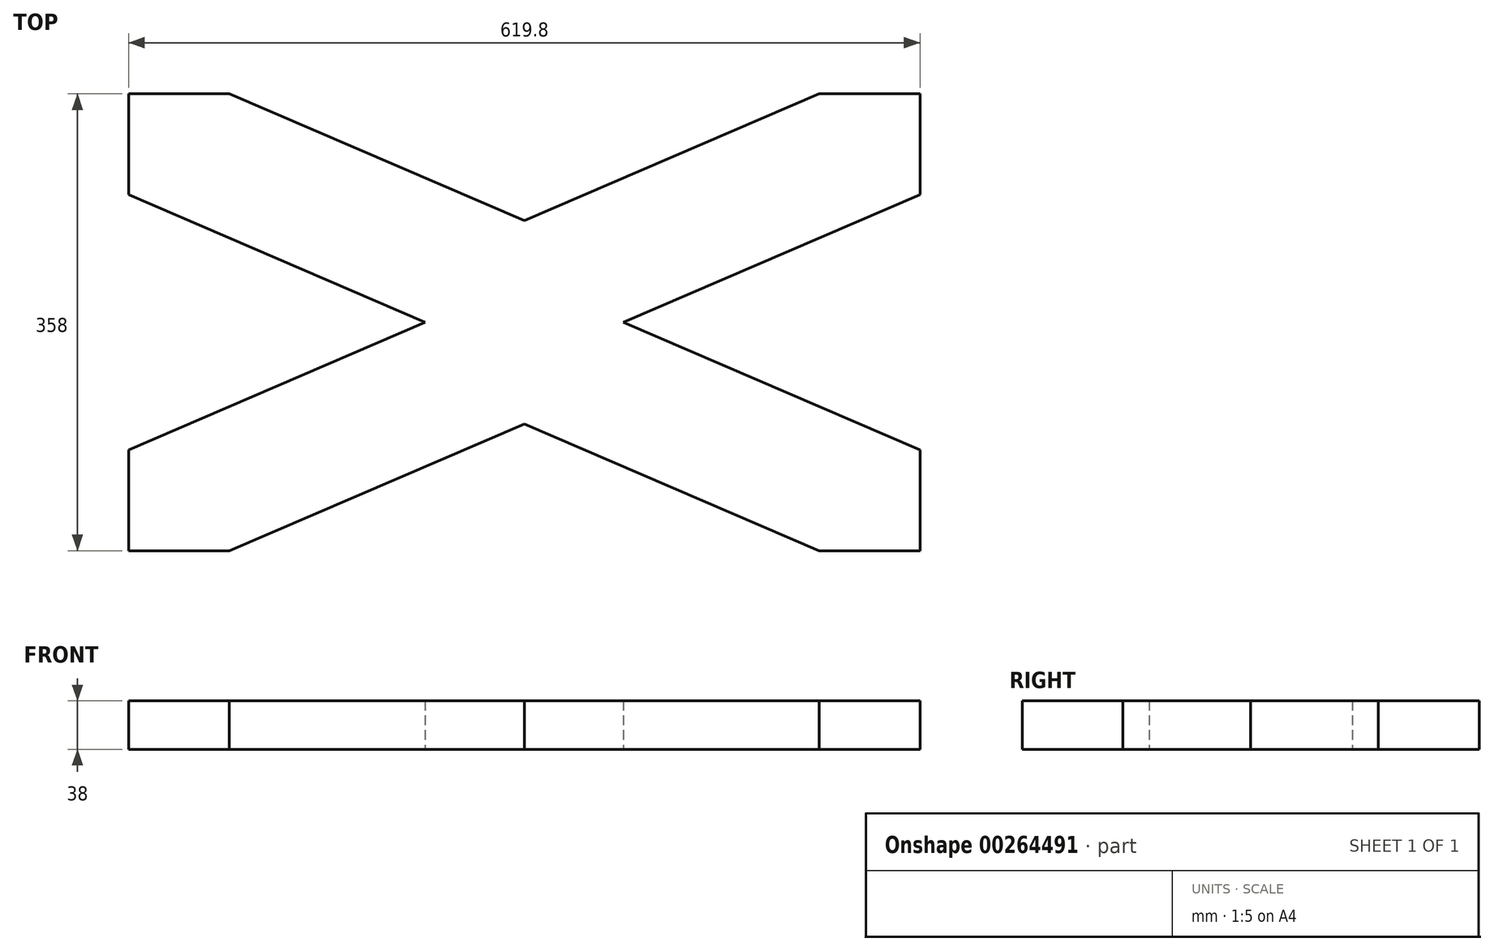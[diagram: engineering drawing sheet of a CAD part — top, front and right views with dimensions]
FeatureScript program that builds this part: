
annotation { "Feature Type Name" : "Feature", "Feature Type Description" : "" }
export const myFeature = defineFeature(function(context is Context, id is Id, definition is map)
    precondition{}
    {
        {
            var Q0;
            Q0=qCreatedBy(makeId("Top.planeOp"),FACE);
            var sketch = newSketch(context, id + "F0", { "sketchPlane" : qUnion([Q0])});
            skLineSegment(sketch, "E0.bottom", {"start": v(-309.9, 179) * mm, "end": v(309.9, 179) * mm, "construction": true});
            skLineSegment(sketch, "E0.top", {"start": v(-309.9, -179) * mm, "end": v(309.9, -179) * mm, "construction": true});
            skLineSegment(sketch, "E0.left", {"start": v(-309.9, 179) * mm, "end": v(-309.9, -179) * mm, "construction": true});
            skLineSegment(sketch, "E0.right", {"start": v(309.9, 179) * mm, "end": v(309.9, -179) * mm, "construction": true});
            skLineSegment(sketch, "E1", {"start": v(0, 179) * mm, "end": v(0, -179) * mm, "construction": true});
            skLineSegment(sketch, "E2", {"start": v(-309.9, 0) * mm, "end": v(309.9, 0) * mm, "construction": true});
            skLineSegment(sketch, "E3", {"start": v(-309.9, -100) * mm, "end": v(-309.9, -179) * mm});
            skLineSegment(sketch, "E4", {"start": v(-309.9, -179) * mm, "end": v(-230.9, -179) * mm});
            skLineSegment(sketch, "E5", {"start": v(-230.9, -179) * mm, "end": v(0, -79.65) * mm});
            skLineSegment(sketch, "E6", {"start": v(0, -79.65) * mm, "end": v(230.9, -179) * mm});
            skLineSegment(sketch, "E7", {"start": v(230.9, -179) * mm, "end": v(309.9, -179) * mm});
            skLineSegment(sketch, "E8", {"start": v(309.9, -100) * mm, "end": v(77.5, 0) * mm});
            skLineSegment(sketch, "E9", {"start": v(77.5, 0) * mm, "end": v(309.9, 100) * mm});
            skLineSegment(sketch, "E10", {"start": v(309.9, 100) * mm, "end": v(309.9, 179) * mm});
            skLineSegment(sketch, "E11", {"start": v(230.9, 179) * mm, "end": v(0, 79.65) * mm});
            skLineSegment(sketch, "E12", {"start": v(0, 79.65) * mm, "end": v(-230.9, 179) * mm});
            skLineSegment(sketch, "E13", {"start": v(-230.9, 179) * mm, "end": v(-309.9, 179) * mm});
            skLineSegment(sketch, "E14", {"start": v(-309.9, 100) * mm, "end": v(-77.5, 0) * mm});
            skLineSegment(sketch, "E15", {"start": v(-77.5, 0) * mm, "end": v(-309.9, -100) * mm});
            skLineSegment(sketch, "E16", {"start": v(-309.9, 100) * mm, "end": v(-309.9, 179) * mm});
            skLineSegment(sketch, "E17", {"start": v(230.9, 179) * mm, "end": v(309.9, 179) * mm});
            skLineSegment(sketch, "E18", {"start": v(309.9, -100) * mm, "end": v(309.9, -179) * mm});
            skSolve(sketch);
        }
        {
            var Q0;
            Q0 = qSketchRegion(id + "F0", true);
            extrude(context, id + "F1", {"entities" : qUnion([Q0]), "depth" : 38 * mm});
        }
    });
